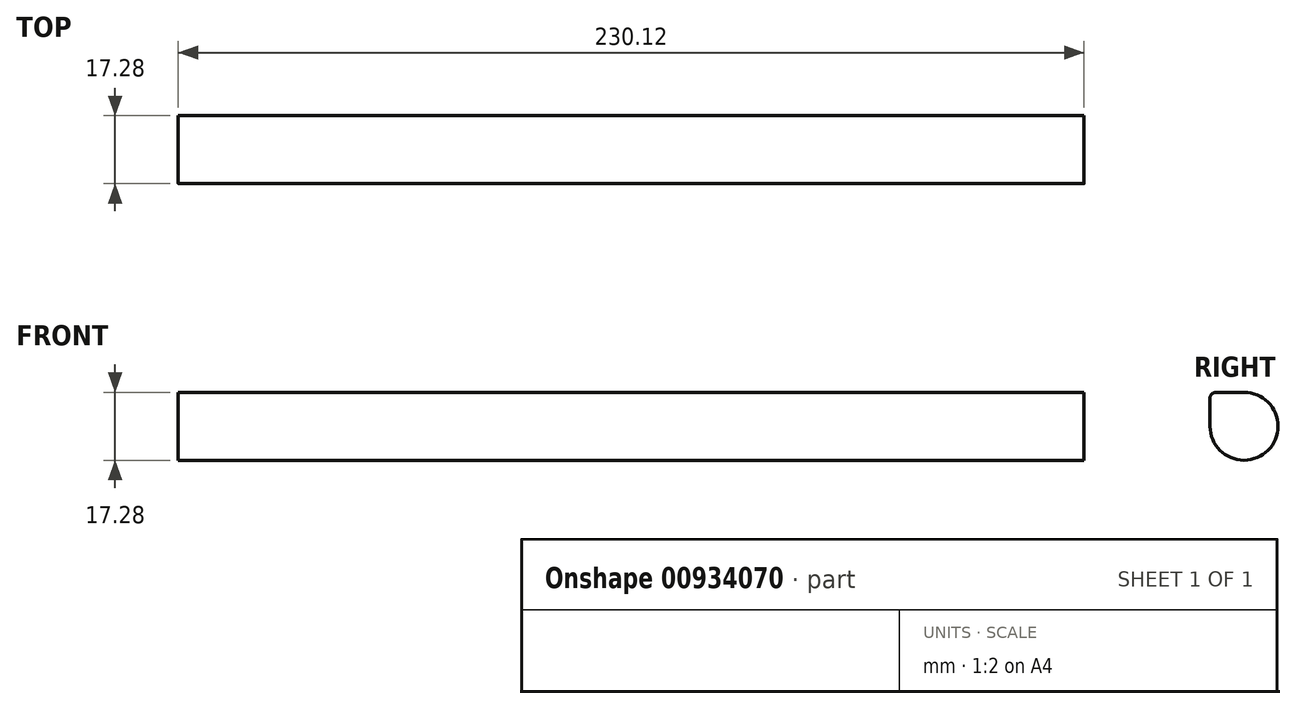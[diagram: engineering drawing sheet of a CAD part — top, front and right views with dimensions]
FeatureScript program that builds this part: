
annotation { "Feature Type Name" : "Feature", "Feature Type Description" : "" }
export const myFeature = defineFeature(function(context is Context, id is Id, definition is map)
    precondition{}
    {
        {
            var Q0;
            Q0=qCreatedBy(makeId("Right.planeOp"),FACE);
            var sketch = newSketch(context, id + "F0", { "sketchPlane" : qUnion([Q0])});
            skArc(sketch, "E0", {"start": v(-8.64, 0) * mm, "mid": v(6.1, -6.1) * mm, "end": v(0, 8.64) * mm});
            skLineSegment(sketch, "E1", {"start": v(0, 8.64) * mm, "end": v(-7.11, 8.64) * mm});
            skLineSegment(sketch, "E2", {"start": v(-8.64, 0) * mm, "end": v(-8.64, 7.11) * mm});
            skPoint(sketch, "E3.visualSharp", {"position": v(-8.64, 8.64) * mm});
            skArc(sketch, "E3.filletArc", {"start": v(-7.11, 8.64) * mm, "mid": v(-8.19, 8.19) * mm, "end": v(-8.64, 7.11) * mm});
            skSolve(sketch);
        }
        {
            var Q0;
            Q0=makeQuery(id+"F0.imprint","IMPRINT",FACE,{"disambiguationData":[TD([[makeQuery(id+"F0.imprint","IMPRINT",EDGE,{"derivedFrom":sQuery(id+"F0.wireOp",EDGE,"E0")}),1.0]])]});
            extrude(context, id + "F1", {"entities" : qUnion([Q0]), "depth" : 230.12 * mm, "offsetDistance" : 25.4 * mm});
        }
    });
